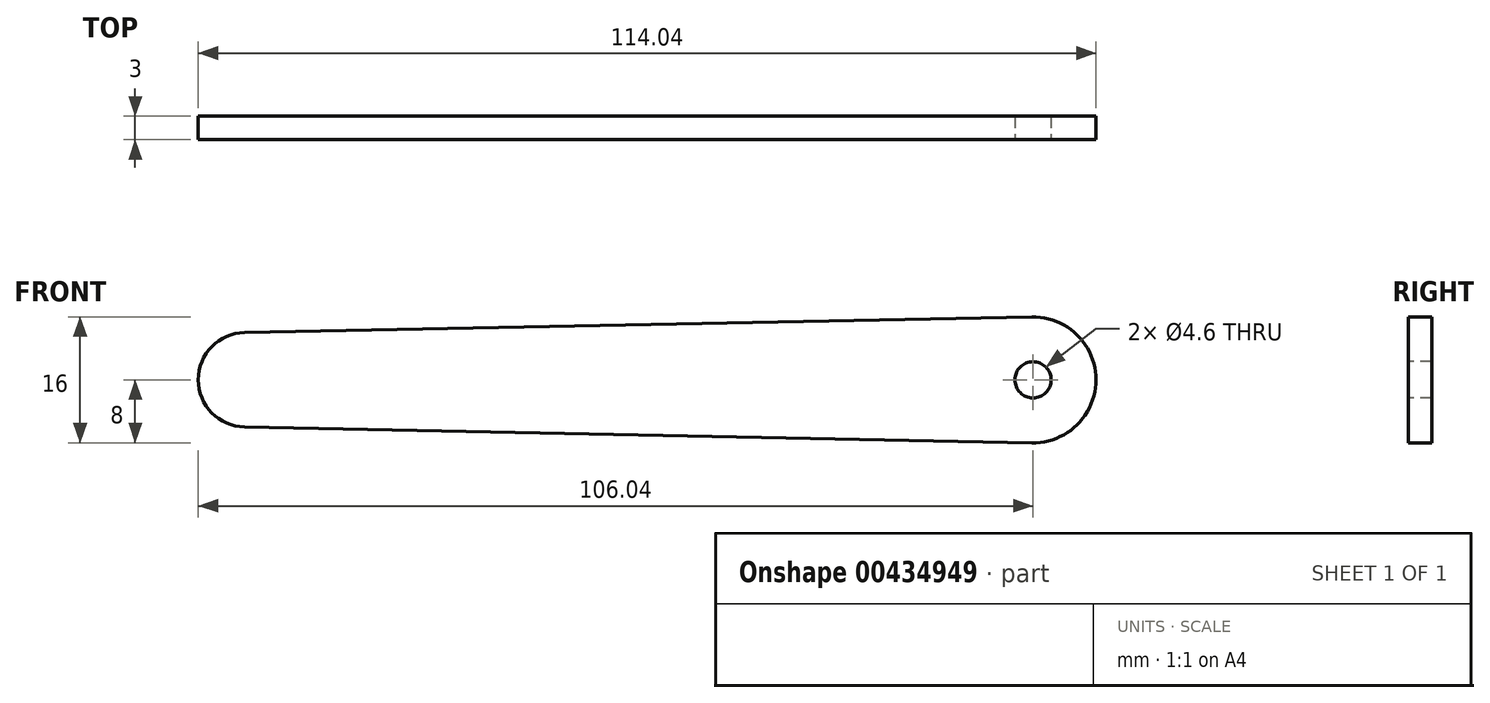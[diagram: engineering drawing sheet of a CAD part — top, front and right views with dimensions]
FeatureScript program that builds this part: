
annotation { "Feature Type Name" : "Feature", "Feature Type Description" : "" }
export const myFeature = defineFeature(function(context is Context, id is Id, definition is map)
    precondition{}
    {
        {
            var Q0;
            Q0=qCreatedBy(makeId("Front.planeOp"),FACE);
            var sketch = newSketch(context, id + "F0", { "sketchPlane" : qUnion([Q0])});
            skLineSegment(sketch, "E0", {"start": v(-50.14, -6) * mm, "end": v(49.86, -8) * mm});
            skLineSegment(sketch, "E1", {"start": v(49.86, 8) * mm, "end": v(-50.14, 6) * mm});
            skArc(sketch, "E2", {"start": v(49.86, -8) * mm, "mid": v(58.02, 0) * mm, "end": v(49.86, 8) * mm});
            skArc(sketch, "E3", {"start": v(-50.14, -6) * mm, "mid": v(-56.02, 0) * mm, "end": v(-50.14, 6) * mm});
            skSolve(sketch);
        }
        {
            var Q0;
            Q0=makeQuery(id+"F0.imprint","IMPRINT",FACE,{"disambiguationData":[TD([[makeQuery(id+"F0.imprint","IMPRINT",EDGE,{"derivedFrom":sQuery(id+"F0.wireOp",EDGE,"E0")}),1.0]])]});
            extrude(context, id + "F1", {"entities" : qUnion([Q0]), "endBound" : BoundingType.SYMMETRIC, "depth" : 3 * mm});
        }
        {
            var Q0;
            Q0=makeQuery(id+"F1.opExtrude","CAP_FACE",FACE,{"disambiguationData":[OSD([sQuery(id+"F0.wireOp",EDGE,"E0"),sQuery(id+"F0.wireOp",EDGE,"E1"),sQuery(id+"F0.wireOp",EDGE,"E2"),sQuery(id+"F0.wireOp",EDGE,"E3")])],"isStart":false});
            var sketch = newSketch(context, id + "F2", { "sketchPlane" : qUnion([Q0])});
            skCircle(sketch, "E4", {"center": v(50.02, 0) * mm, "radius": 2.3 * mm});
            skSolve(sketch);
        }
        {
            var Q0;
            Q0=makeQuery(id+"F2.imprint","IMPRINT",FACE,{"disambiguationData":[TD([[makeQuery(id+"F2.imprint","IMPRINT",EDGE,{"derivedFrom":sQuery(id+"F2.wireOp",EDGE,"E4")}),1.0]])]});
            extrude(context, id + "F3", {"entities" : qUnion([Q0]), "operationType" : NewBodyOperationType.REMOVE, "oppositeDirection" : true, "depth" : 25 * mm});
        }
    });
